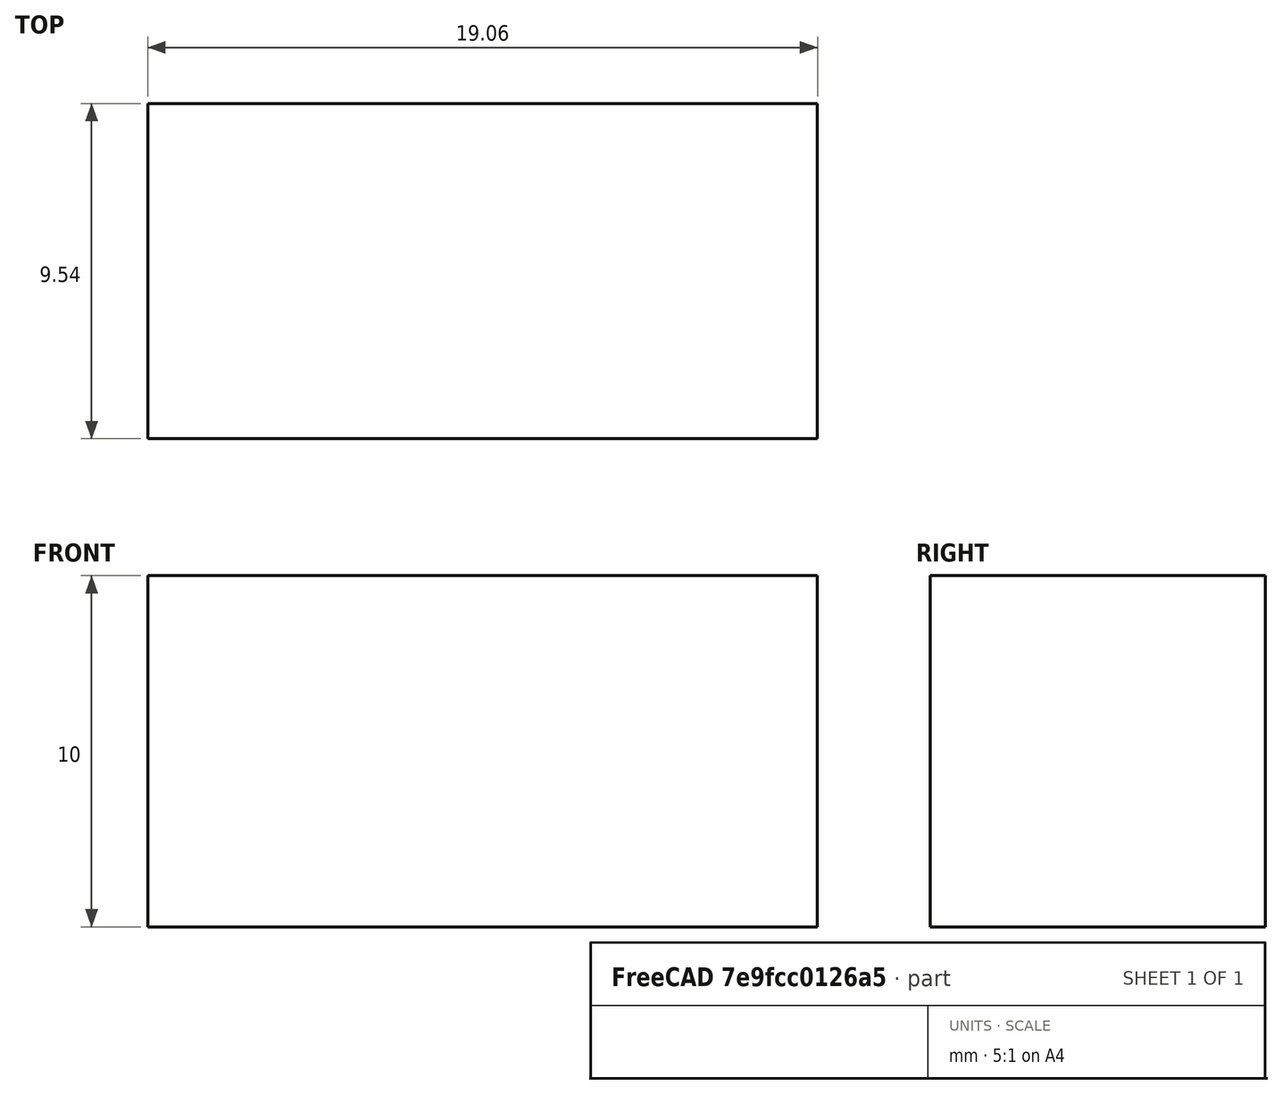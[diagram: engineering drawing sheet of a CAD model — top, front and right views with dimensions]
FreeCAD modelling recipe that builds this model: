
FCSTD DOCUMENT  (FreeCAD 0.21R39043 (Git))
Label: waveguide2
License: All rights reserved
LicenseURL: https://en.wikipedia.org/wiki/All_rights_reserved
objects: Sketcher::SketchObject×2, PartDesign::Body×2, PartDesign::Pad×1, Part::SubShapeBinder×1, PartDesign::Extrusion×1, App::Part×1
note: 13 computed .brp shape members not serialized (recipe doc carries the construction recipe); baked Part::Feature solids carry a one-line shape summary decoded from their .brp

FEATURE [Sketcher::SketchObject] Sketch
  ArcFitTolerance = 1e-06
  AttachmentSupport = -> [XZ_Plane]
  ExternalBSplineMaxDegree = 5
  ExternalBSplineTolerance = 0.0001
  FixShape = 1
  FullyConstrained = true
  InternalTolerance = 1e-06
  InvalidShape = false
  MakeInternals = false
  MapMode = 5
  Placement = pos=(0,0,0) rot=(1,0,0;1.5708rad)
  Support = -> [XZ_Plane]
  TreeRank = 14
  ValidateShape = false
  sketch-geometry (4):
    g0: LineSegment StartX=-9.525 StartY=5 StartZ=0 EndX=9.525 EndY=5 EndZ=0
    g1: LineSegment StartX=9.525 StartY=5 StartZ=0 EndX=9.525 EndY=-5 EndZ=0
    g2: LineSegment StartX=9.525 StartY=-5 StartZ=0 EndX=-9.525 EndY=-5 EndZ=0
    g3: LineSegment StartX=-9.525 StartY=-5 StartZ=0 EndX=-9.525 EndY=5 EndZ=0
  constraints (11):
    c: Coincident(g0,g1)
    c: Coincident(g1,g2)
    c: Coincident(g2,g3)
    c: Coincident(g3,g0)
    c: Horizontal(g0)
    c: Horizontal(g2)
    c: Vertical(g1)
    c: DistanceY(g3,g3) = 10
    c: DistanceX(g2,g2) = 19.05
    c: Vertical(g3)
    c: Symmetric(g0,g2,g-1)
FEATURE [PartDesign::Pad] Pad
  AddSubType = 0
  AlongSketchNormal = false
  AutoTaperInnerAngle = true
  CheckUpToFaceLimits = true
  ClaimChildren = false
  Direction = (0,-1,0)
  Fit = 0
  FitJoin = 0
  FixShape = 1
  InnerFit = 0
  InnerFitJoin = 0
  InvalidShape = false
  Length = 9.54
  Length2 = 10
  Linearize = true
  NewSolid = false
  Profile = -> Sketch
  ReferenceAxis = -> Sketch [N_Axis]
  Suppress = false
  TaperInnerAngle = 0
  TaperInnerAngleRev = 0
  TreeRank = 15
  Type = 0
  ValidateShape = true
  _ProfileBasedVersion = 1
FEATURE [PartDesign::Body] Body  label="DIEL_CAVITY"
  AutoGroupSolids = false
  ClaimAllChildren = false
  ExportMode = 0
  FixShape = 1
  Group = -> [Sketch,Pad]
  InvalidShape = false
  Origin = -> Origin001
  Tip = -> Pad
  TreeRank = 13
  ValidateShape = false
  _ExportChildren = -> [Pad]
  _GroupVersion = 1
FEATURE [Part::SubShapeBinder] Import  label="Import(Pad)"
  BindCopyOnChange = 0
  BindMode = 0
  ClaimChildren = false
  Context = -> Part [Body001.Import.]
  EdgeTolerance = 1e-06
  FillStyle = 0
  FixShape = 1
  Fuse = false
  Group_EnableExport = false
  InvalidShape = false
  MakeFace = false
  MergeEdges = true
  OffsetFill = false
  OffsetIntersection = false
  OffsetJoinType = 0
  OffsetOpenResult = false
  Outline = false
  PartialLoad = false
  Relative = true
  SplitEdges = false
  Support = -> [Body[Pad.]]
  TightBound = false
  TreeRank = 26
  ValidateShape = false
  _Version = 8
FEATURE [Sketcher::SketchObject] Sketch001
  ArcFitTolerance = 1e-06
  AttachmentSupport = -> [Import]
  ExternalBSplineMaxDegree = 5
  ExternalBSplineTolerance = 0.0001
  ExternalGeometry = -> [Import]
  FixShape = 1
  FullyConstrained = true
  Group_EnableExport = false
  InternalTolerance = 1e-06
  InvalidShape = false
  MakeInternals = false
  MapMode = 5
  Placement = pos=(0,-1.1e-15,-5) rot=(1,0,0;3.14159rad)
  Support = -> [Import]
  TreeRank = 27
  ValidateShape = false
  sketch-geometry (1):
    g0: LineSegment StartX=-9.525 StartY=4.77 StartZ=0 EndX=9.525 EndY=4.77 EndZ=0
  constraints (2):
    c: Symmetric(g-3,g-3,g0)
    c: Symmetric(g-4,g-4,g0)
FEATURE [PartDesign::Extrusion] Extrusion
  AddSubType = 0
  AlongSketchNormal = false
  AutoTaperInnerAngle = true
  CheckUpToFaceLimits = true
  ClaimChildren = false
  Direction = (0,-2e-16,-1)
  Fit = 0
  FitJoin = 0
  FixShape = 1
  Group_EnableExport = true
  InnerFit = 0
  InnerFitJoin = 0
  InvalidShape = false
  Length = 10
  Length2 = 10
  Linearize = true
  NewSolid = false
  Profile = -> Sketch001
  ReferenceAxis = -> Sketch001 [N_Axis]
  Reversed = true
  Suppress = false
  TaperInnerAngle = 0
  TaperInnerAngleRev = 0
  TreeRank = 28
  Type = 0
  ValidateShape = true
  _ProfileBasedVersion = 1
FEATURE [PartDesign::Body] Body001  label="SPLIT_1"
  AutoGroupSolids = false
  ClaimAllChildren = false
  ExportMode = 2
  FixShape = 1
  Group = -> [Import,Sketch001,Extrusion]
  InvalidShape = false
  Origin = -> Origin002
  TreeRank = 25
  ValidateShape = false
  _ExportChildren = -> [Import,Sketch001,Extrusion]
  _GroupVersion = 1
FEATURE [App::Part] Part  label="CMP_waveguide2"
  ClaimAllChildren = false
  ExportMode = 1
  Group = -> [Body,Body001]
  Origin = -> Origin
  TreeRank = 3
  _ExportChildren = -> [Body,Body001]
  _GroupVersion = 1
